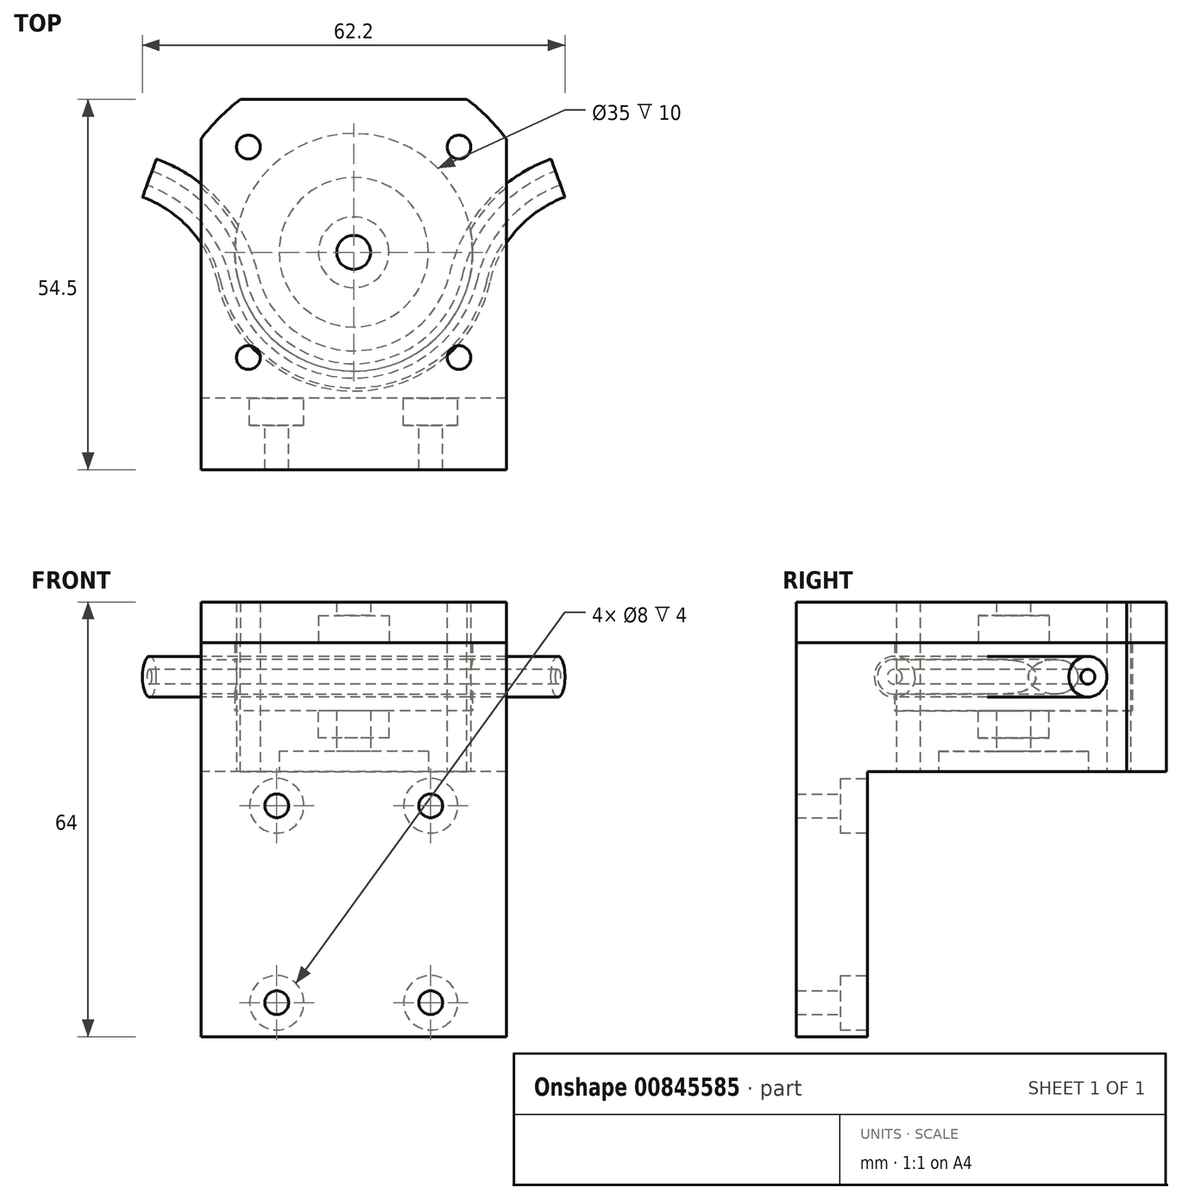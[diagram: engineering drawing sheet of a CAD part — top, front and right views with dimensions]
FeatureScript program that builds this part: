
annotation { "Feature Type Name" : "Feature", "Feature Type Description" : "" }
export const myFeature = defineFeature(function(context is Context, id is Id, definition is map)
    precondition{}
    {
        {
            var Q0;
            Q0=qCreatedBy(makeId("Top.planeOp"),FACE);
            var sketch = newSketch(context, id + "F0", { "sketchPlane" : qUnion([Q0])});
            skLineSegment(sketch, "E0", {"start": v(-21.5, -16.33) * mm, "end": v(-21.5, 16.33) * mm});
            skLineSegment(sketch, "E1", {"start": v(-16.33, 21.5) * mm, "end": v(16.33, 21.5) * mm});
            skLineSegment(sketch, "E2", {"start": v(21.5, 16.33) * mm, "end": v(21.5, -16.33) * mm});
            skLineSegment(sketch, "E3", {"start": v(16.33, -21.5) * mm, "end": v(-16.33, -21.5) * mm});
            skArc(sketch, "E4", {"start": v(-16.33, 21.5) * mm, "mid": v(-19.1, 19.1) * mm, "end": v(-21.5, 16.33) * mm});
            skArc(sketch, "E5", {"start": v(21.5, 16.33) * mm, "mid": v(19.1, 19.1) * mm, "end": v(16.33, 21.5) * mm});
            skCircle(sketch, "E6", {"center": v(-15.5, 15.5) * mm, "radius": 1.75 * mm});
            skCircle(sketch, "E7", {"center": v(15.5, 15.5) * mm, "radius": 1.75 * mm});
            skCircle(sketch, "E8", {"center": v(0, 0) * mm, "radius": 11 * mm});
            skCircle(sketch, "E9", {"center": v(-15.5, -15.5) * mm, "radius": 1.75 * mm});
            skCircle(sketch, "E10", {"center": v(15.5, -15.5) * mm, "radius": 1.75 * mm});
            skArc(sketch, "E11", {"start": v(-21.5, -16.33) * mm, "mid": v(-19.1, -19.1) * mm, "end": v(-16.33, -21.5) * mm});
            skArc(sketch, "E12", {"start": v(16.33, -21.5) * mm, "mid": v(19.1, -19.1) * mm, "end": v(21.5, -16.33) * mm});
            skLineSegment(sketch, "E13.bottom", {"start": v(15.5, 15.5) * mm, "end": v(-15.5, 15.5) * mm, "construction": true});
            skLineSegment(sketch, "E13.top", {"start": v(15.5, -15.5) * mm, "end": v(-15.5, -15.5) * mm, "construction": true});
            skLineSegment(sketch, "E13.left", {"start": v(15.5, 15.5) * mm, "end": v(15.5, -15.5) * mm, "construction": true});
            skLineSegment(sketch, "E13.right", {"start": v(-15.5, 15.5) * mm, "end": v(-15.5, -15.5) * mm, "construction": true});
            skLineSegment(sketch, "E14", {"start": v(0, 21.5) * mm, "end": v(0, -21.5) * mm, "construction": true});
            skLineSegment(sketch, "E15", {"start": v(-21.5, 0) * mm, "end": v(21.5, 0) * mm, "construction": true});
            skPoint(sketch, "E15.endSnap0", {"position": v(21.5, 0) * mm});
            skCircle(sketch, "E16", {"center": v(0, 0) * mm, "radius": 2.5 * mm});
            skSolve(sketch);
        }
        {
            var Q0;
            Q0=makeQuery(id+"F0.imprint","IMPRINT",FACE,{"disambiguationData":[TD([[makeQuery(id+"F0.imprint","IMPRINT",EDGE,{"derivedFrom":sQuery(id+"F0.wireOp",EDGE,"E0")}),-1.0]])]});
            var Q1;
            Q1=makeQuery(id+"F0.imprint","IMPRINT",FACE,{"disambiguationData":[TD([[makeQuery(id+"F0.imprint","IMPRINT",EDGE,{"derivedFrom":sQuery(id+"F0.wireOp",EDGE,"E8")}),1.0]])]});
            extrude(context, id + "F1", {"entities" : qUnion([Q0, Q1]), "depth" : 2 * mm, "offsetDistance" : 25 * mm});
        }
        {
            var Q0;
            Q0=makeQuery(id+"F1.opExtrude","CAP_FACE",FACE,{"disambiguationData":[OSD([sQuery(id+"F0.wireOp",EDGE,"E0"),sQuery(id+"F0.wireOp",EDGE,"E1"),sQuery(id+"F0.wireOp",EDGE,"E2"),sQuery(id+"F0.wireOp",EDGE,"E3"),sQuery(id+"F0.wireOp",EDGE,"E4"),sQuery(id+"F0.wireOp",EDGE,"E5"),sQuery(id+"F0.wireOp",EDGE,"E6"),sQuery(id+"F0.wireOp",EDGE,"E7"),sQuery(id+"F0.wireOp",EDGE,"E8"),sQuery(id+"F0.wireOp",EDGE,"E9"),sQuery(id+"F0.wireOp",EDGE,"E10"),sQuery(id+"F0.wireOp",EDGE,"E11"),sQuery(id+"F0.wireOp",EDGE,"E12")])],"isStart":false});
            var Q1;
            Q1=makeQuery(id+"F0.imprint","IMPRINT",FACE,{"disambiguationData":[TD([[makeQuery(id+"F0.imprint","IMPRINT",EDGE,{"derivedFrom":sQuery(id+"F0.wireOp",EDGE,"d85fea0c-31e0-45f3-b9b2-28f0fcc0159b")}),-1.0]])]});
            extrude(context, id + "F2", {"entities" : qUnion([Q0, Q1]), "operationType" : NewBodyOperationType.ADD, "depth" : 7 * mm, "offsetDistance" : 25 * mm});
        }
        {
            var Q0;
            Q0=makeQuery(id+"F2.opExtrude","CAP_FACE",FACE,{"disambiguationData":[OSD([sQuery(id+"F0.wireOp",EDGE,"E0"),sQuery(id+"F0.wireOp",EDGE,"E1"),sQuery(id+"F0.wireOp",EDGE,"E2"),sQuery(id+"F0.wireOp",EDGE,"E3"),sQuery(id+"F0.wireOp",EDGE,"E4"),sQuery(id+"F0.wireOp",EDGE,"E5"),sQuery(id+"F0.wireOp",EDGE,"E6"),sQuery(id+"F0.wireOp",EDGE,"E7"),sQuery(id+"F0.wireOp",EDGE,"E8"),sQuery(id+"F0.wireOp",EDGE,"E9"),sQuery(id+"F0.wireOp",EDGE,"E10"),sQuery(id+"F0.wireOp",EDGE,"E11"),sQuery(id+"F0.wireOp",EDGE,"E12")])],"isStart":false});
            var sketch = newSketch(context, id + "F3", { "sketchPlane" : qUnion([Q0])});
            skArc(sketch, "E17.0", {"start": v(-16.67, 22.5) * mm, "mid": v(-19.8, 19.8) * mm, "end": v(-22.5, 16.67) * mm});
            skLineSegment(sketch, "E17.1", {"start": v(-22.5, -16.67) * mm, "end": v(-22.5, 16.67) * mm});
            skLineSegment(sketch, "E17.2", {"start": v(-16.67, 22.5) * mm, "end": v(16.67, 22.5) * mm});
            skArc(sketch, "E17.3", {"start": v(-22.5, -16.67) * mm, "mid": v(-19.8, -19.8) * mm, "end": v(-16.67, -22.5) * mm});
            skArc(sketch, "E17.4", {"start": v(22.5, 16.67) * mm, "mid": v(19.8, 19.8) * mm, "end": v(16.67, 22.5) * mm});
            skLineSegment(sketch, "E17.5", {"start": v(22.5, 16.67) * mm, "end": v(22.5, -16.67) * mm});
            skArc(sketch, "E17.6", {"start": v(16.67, -22.5) * mm, "mid": v(19.8, -19.8) * mm, "end": v(22.5, -16.67) * mm});
            skLineSegment(sketch, "E17.7", {"start": v(16.67, -22.5) * mm, "end": v(-16.67, -22.5) * mm});
            skSolve(sketch);
        }
        {
            var Q0;
            Q0=makeQuery(id+"F3.imprint","IMPRINT",FACE,{"disambiguationData":[TD([[makeQuery(id+"F3.imprint","IMPRINT",EDGE,{"derivedFrom":sQuery(id+"F3.wireOp",EDGE,"E17.0")}),1.0]])]});
            extrude(context, id + "F4", {"entities" : qUnion([Q0]), "operationType" : NewBodyOperationType.ADD, "oppositeDirection" : true, "depth" : 48 * mm, "offsetDistance" : 25 * mm});
        }
        {
            var Q0;
            {var subQ0=sQuery(id+"F0.wireOp",EDGE,"E12");var subQ1=sQuery(id+"F0.wireOp",EDGE,"E11");var subQ2=sQuery(id+"F0.wireOp",EDGE,"E5");var subQ3=sQuery(id+"F0.wireOp",EDGE,"E4");var subQ4=sQuery(id+"F0.wireOp",EDGE,"E3");var subQ5=sQuery(id+"F0.wireOp",EDGE,"E2");var subQ6=sQuery(id+"F0.wireOp",EDGE,"E1");var subQ7=sQuery(id+"F0.wireOp",EDGE,"E0");Q0=makeQuery(id+"F4.boolean.opBoolean","MERGE",FACE,{"derivedFrom":[makeQuery(id+"F2.opExtrude","CAP_FACE",FACE,{"disambiguationData":[OSD([subQ7,subQ6,subQ5,subQ4,subQ3,subQ2,sQuery(id+"F0.wireOp",EDGE,"E6"),sQuery(id+"F0.wireOp",EDGE,"E7"),sQuery(id+"F0.wireOp",EDGE,"E8"),sQuery(id+"F0.wireOp",EDGE,"E9"),sQuery(id+"F0.wireOp",EDGE,"E10"),subQ1,subQ0])],"isStart":false}),makeQuery(id+"F4.opExtrude","CAP_FACE",FACE,{"disambiguationData":[OSD([subQ7,subQ6,subQ5,subQ4,subQ3,subQ2,subQ1,subQ0,sQuery(id+"F3.wireOp",EDGE,"E17.0"),sQuery(id+"F3.wireOp",EDGE,"E17.1"),sQuery(id+"F3.wireOp",EDGE,"E17.2"),sQuery(id+"F3.wireOp",EDGE,"E17.3"),sQuery(id+"F3.wireOp",EDGE,"E17.4"),sQuery(id+"F3.wireOp",EDGE,"E17.5"),sQuery(id+"F3.wireOp",EDGE,"E17.6"),sQuery(id+"F3.wireOp",EDGE,"E17.7")])],"isStart":true})]});}
            var sketch = newSketch(context, id + "F5", { "sketchPlane" : qUnion([Q0])});
            skCircle(sketch, "E18", {"center": v(0, 0) * mm, "radius": 32 * mm});
            skLineSegment(sketch, "E19", {"start": v(-22.5, -16.67) * mm, "end": v(-22.5, -32) * mm});
            skLineSegment(sketch, "E20", {"start": v(-22.5, -32) * mm, "end": v(22.5, -32) * mm});
            skLineSegment(sketch, "E21", {"start": v(22.5, -32) * mm, "end": v(22.5, -16.67) * mm});
            skCircle(sketch, "E22", {"center": v(0, 0) * mm, "radius": 17.5 * mm});
            skCircle(sketch, "E23", {"center": v(0, 0) * mm, "radius": 2.5 * mm});
            skSolve(sketch);
        }
        {
            var Q0;
            {var subQ1=sQuery(id+"F5.wireOp",EDGE,"E21");Q0=makeQuery(id+"F5.imprint","IMPRINT",FACE,{"disambiguationData":[TD([[makeQuery(id+"F5.imprint","IMPRINT",EDGE,{"derivedFrom":subQ1}),1.0]])]});}
            var Q1;
            {var subQ1=sQuery(id+"F5.wireOp",EDGE,"E19");Q1=makeQuery(id+"F5.imprint","IMPRINT",FACE,{"disambiguationData":[TD([[makeQuery(id+"F5.imprint","IMPRINT",EDGE,{"derivedFrom":subQ1}),1.0]])]});}
            var Q2;
            {var subQ0=sQuery(id+"F5.wireOp",EDGE,"E18");var subQ1=makeQuery(id+"F5.imprint","INTERSECT",VERTEX,{"derivedFrom":[subQ0,sQuery(id+"F5.wireOp",EDGE,"E20")]});Q2=makeQuery(id+"F5.imprint","IMPRINT",FACE,{"disambiguationData":[TD([[makeQuery(id+"F5.imprint","IMPRINT",EDGE,{"disambiguationData":[TD([[subQ1,1.0]])],"derivedFrom":subQ0}),1.0]])]});}
            extrude(context, id + "F6", {"entities" : qUnion([Q0, Q1, Q2]), "operationType" : NewBodyOperationType.ADD, "oppositeDirection" : true, "depth" : 48 * mm, "offsetDistance" : 25 * mm});
        }
        {
            var Q0;
            {var subQ4=sQuery(id+"F5.wireOp",EDGE,"E18");var subQ28=makeQuery(id+"F4.opExtrude","CAP_EDGE",EDGE,{"disambiguationData":[OSD([sQuery(id+"F3.wireOp",EDGE,"646ab015-f94a-48a6-a4ab-2b46942ccab2.2")])],"isStart":true});var subQ29=makeQuery(id+"F5.imprint","INTERSECT",VERTEX,{"derivedFrom":[subQ28,subQ4]});Q0=makeQuery(id+"F5.imprint","IMPRINT",FACE,{"disambiguationData":[TD([[makeQuery(id+"F5.imprint","IMPRINT",EDGE,{"disambiguationData":[TD([[subQ29,-1.0]])],"derivedFrom":subQ4}),1.0]])]});}
            var Q1;
            {var subQ0=sQuery(id+"F5.wireOp",EDGE,"E18");var subQ1=makeQuery(id+"F4.boolean.opBoolean","MERGE",EDGE,{"derivedFrom":[makeQuery(id+"F2.opExtrude","CAP_EDGE",EDGE,{"disambiguationData":[OSD([sQuery(id+"F1Hpu5VrwMmlooL_1.wireOp",EDGE,"8e26481d-0692-495c-8b6e-13f98c5af57d")])],"isStart":false}),makeQuery(id+"F4.opExtrude","CAP_EDGE",EDGE,{"disambiguationData":[OSD([sQuery(id+"F3.wireOp",EDGE,"JSha1XCR-3J3x-jMRG-RlZc-dtnEwsOd18PA")])],"isStart":true}),makeQuery(id+"F4.opExtrude","CAP_EDGE",EDGE,{"disambiguationData":[OSD([sQuery(id+"F3.wireOp",EDGE,"9211a1b2-c39d-4ab5-b8c2-9bb960df69d4.trimOffspring")])],"isStart":true})]});var subQ2=makeQuery(id+"F5.imprint","INTERSECT",VERTEX,{"disambiguationData":[OD(0.0)],"derivedFrom":[subQ1,subQ0]});Q1=makeQuery(id+"F5.imprint","IMPRINT",FACE,{"disambiguationData":[TD([[makeQuery(id+"F5.imprint","IMPRINT",EDGE,{"disambiguationData":[TD([[subQ2,-1.0]])],"derivedFrom":subQ0}),1.0]])]});}
            var Q2;
            {var subQ0=sQuery(id+"F5.wireOp",EDGE,"E18");var subQ1=makeQuery(id+"F4.opExtrude","CAP_EDGE",EDGE,{"disambiguationData":[OSD([sQuery(id+"F3.wireOp",EDGE,"646ab015-f94a-48a6-a4ab-2b46942ccab2.4")])],"isStart":true});var subQ2=makeQuery(id+"F5.imprint","INTERSECT",VERTEX,{"derivedFrom":[subQ1,subQ0]});Q2=makeQuery(id+"F5.imprint","IMPRINT",FACE,{"disambiguationData":[TD([[makeQuery(id+"F5.imprint","IMPRINT",EDGE,{"disambiguationData":[TD([[subQ2,-1.0]])],"derivedFrom":subQ0}),1.0]])]});}
            var Q3;
            {var subQ6=sQuery(id+"F5.wireOp",EDGE,"E19");Q3=makeQuery(id+"F5.imprint","IMPRINT",FACE,{"disambiguationData":[TD([[makeQuery(id+"F5.imprint","IMPRINT",EDGE,{"derivedFrom":subQ6}),1.0]])]});}
            var Q4;
            {var subQ0=sQuery(id+"F5.wireOp",EDGE,"E18");var subQ1=makeQuery(id+"F5.imprint","INTERSECT",VERTEX,{"derivedFrom":[subQ0,sQuery(id+"F5.wireOp",EDGE,"E20")]});Q4=makeQuery(id+"F5.imprint","IMPRINT",FACE,{"disambiguationData":[TD([[makeQuery(id+"F5.imprint","IMPRINT",EDGE,{"disambiguationData":[TD([[subQ1,1.0]])],"derivedFrom":subQ0}),1.0]])]});}
            var Q5;
            {var subQ6=sQuery(id+"F5.wireOp",EDGE,"E21");Q5=makeQuery(id+"F5.imprint","IMPRINT",FACE,{"disambiguationData":[TD([[makeQuery(id+"F5.imprint","IMPRINT",EDGE,{"derivedFrom":subQ6}),1.0]])]});}
            var Q6;
            {var subQ0=sQuery(id+"F5.wireOp",EDGE,"E18");var subQ1=makeQuery(id+"F4.opExtrude","CAP_EDGE",EDGE,{"disambiguationData":[OSD([sQuery(id+"F3.wireOp",EDGE,"646ab015-f94a-48a6-a4ab-2b46942ccab2.7")])],"isStart":true});var subQ2=makeQuery(id+"F5.imprint","INTERSECT",VERTEX,{"disambiguationData":[OD(0.0)],"derivedFrom":[subQ1,subQ0]});Q6=makeQuery(id+"F5.imprint","IMPRINT",FACE,{"disambiguationData":[TD([[makeQuery(id+"F5.imprint","IMPRINT",EDGE,{"disambiguationData":[TD([[subQ2,1.0]])],"derivedFrom":subQ0}),1.0]])]});}
            var Q7;
            {var subQ0=sQuery(id+"F5.wireOp",EDGE,"E22");var subQ1=makeQuery(id+"F2.opExtrude","CAP_EDGE",EDGE,{"disambiguationData":[OSD([sQuery(id+"F1Hpu5VrwMmlooL_1.wireOp",EDGE,"9a130dde-bc44-4270-aeb8-7f362e7485a4")])],"isStart":false});var subQ2=makeQuery(id+"F5.imprint","INTERSECT",VERTEX,{"disambiguationData":[OD(0.0)],"derivedFrom":[subQ1,subQ0]});Q7=makeQuery(id+"F5.imprint","IMPRINT",FACE,{"disambiguationData":[TD([[makeQuery(id+"F5.imprint","IMPRINT",EDGE,{"disambiguationData":[TD([[subQ2,-1.0]])],"derivedFrom":subQ0}),-1.0]])]});}
            var Q8;
            {var subQ0=sQuery(id+"F5.wireOp",EDGE,"E22");var subQ1=makeQuery(id+"F2.opExtrude","CAP_EDGE",EDGE,{"disambiguationData":[OSD([sQuery(id+"F1Hpu5VrwMmlooL_1.wireOp",EDGE,"1fc29757-d1f2-4ccb-9a81-5a1ceaa807c7")])],"isStart":false});var subQ2=makeQuery(id+"F5.imprint","INTERSECT",VERTEX,{"disambiguationData":[OD(0.0)],"derivedFrom":[subQ1,subQ0]});Q8=makeQuery(id+"F5.imprint","IMPRINT",FACE,{"disambiguationData":[TD([[makeQuery(id+"F5.imprint","IMPRINT",EDGE,{"disambiguationData":[TD([[subQ2,-1.0]])],"derivedFrom":subQ0}),-1.0]])]});}
            var Q9;
            {var subQ0=sQuery(id+"F5.wireOp",EDGE,"E22");var subQ1=makeQuery(id+"F2.opExtrude","CAP_EDGE",EDGE,{"disambiguationData":[OSD([sQuery(id+"F1Hpu5VrwMmlooL_1.wireOp",EDGE,"4d534888-ec9c-4465-8bad-2fd676ba325a")])],"isStart":false});var subQ2=makeQuery(id+"F5.imprint","INTERSECT",VERTEX,{"disambiguationData":[OD(0.0)],"derivedFrom":[subQ1,subQ0]});Q9=makeQuery(id+"F5.imprint","IMPRINT",FACE,{"disambiguationData":[TD([[makeQuery(id+"F5.imprint","IMPRINT",EDGE,{"disambiguationData":[TD([[subQ2,1.0]])],"derivedFrom":subQ0}),-1.0]])]});}
            var Q10;
            {var subQ0=sQuery(id+"F5.wireOp",EDGE,"E22");var subQ1=makeQuery(id+"F2.opExtrude","CAP_EDGE",EDGE,{"disambiguationData":[OSD([sQuery(id+"F1Hpu5VrwMmlooL_1.wireOp",EDGE,"5fe68f5a-298d-45ce-920e-f32339d6a1d9")])],"isStart":false});var subQ2=makeQuery(id+"F5.imprint","INTERSECT",VERTEX,{"disambiguationData":[OD(0.0)],"derivedFrom":[subQ1,subQ0]});Q10=makeQuery(id+"F5.imprint","IMPRINT",FACE,{"disambiguationData":[TD([[makeQuery(id+"F5.imprint","IMPRINT",EDGE,{"disambiguationData":[TD([[subQ2,-1.0]])],"derivedFrom":subQ0}),-1.0]])]});}
            var Q11;
            Q11=makeQuery(id+"F5.imprint","IMPRINT",FACE,{"disambiguationData":[TD([[makeQuery(id+"F5.imprint","IMPRINT",EDGE,{"derivedFrom":sQuery(id+"F5.wireOp",EDGE,"E22")}),-1.0]])]});
            extrude(context, id + "F7", {"entities" : qUnion([Q0, Q1, Q2, Q3, Q4, Q5, Q6, Q7, Q8, Q9, Q10, Q11]), "operationType" : NewBodyOperationType.ADD, "depth" : 10 * mm, "offsetDistance" : 25 * mm});
        }
        {
            var Q0;
            {var subQ4=sQuery(id+"F5.wireOp",EDGE,"E18");var subQ28=makeQuery(id+"F4.opExtrude","CAP_EDGE",EDGE,{"disambiguationData":[OSD([sQuery(id+"F3.wireOp",EDGE,"646ab015-f94a-48a6-a4ab-2b46942ccab2.2")])],"isStart":true});var subQ29=makeQuery(id+"F5.imprint","INTERSECT",VERTEX,{"derivedFrom":[subQ28,subQ4]});Q0=makeQuery(id+"F5.imprint","IMPRINT",FACE,{"disambiguationData":[TD([[makeQuery(id+"F5.imprint","IMPRINT",EDGE,{"disambiguationData":[TD([[subQ29,-1.0]])],"derivedFrom":subQ4}),1.0]])]});}
            cPlane(context, id + "F8", {"entities" : qUnion([Q0]), "cplaneType" : CPlaneType.OFFSET, "offset" : 5 * mm, "width" : 150 * mm, "height" : 150 * mm});
        }
        {
            var Q0;
            Q0=qCreatedBy(id+"F8.planeOp",FACE);
            var sketch = newSketch(context, id + "F9", { "sketchPlane" : qUnion([Q0])});
            skArc(sketch, "E24", {"start": v(-17.07, -3.83) * mm, "mid": v(0, -17.5) * mm, "end": v(17.07, -3.83) * mm});
            skArc(sketch, "E25", {"start": v(-17.07, -3.83) * mm, "mid": v(-21.68, 5.22) * mm, "end": v(-30.07, 10.94) * mm});
            skArc(sketch, "E26", {"start": v(30.07, 10.94) * mm, "mid": v(21.68, 5.22) * mm, "end": v(17.07, -3.83) * mm});
            skLineSegment(sketch, "E27", {"start": v(0, 0) * mm, "end": v(30.07, 10.94) * mm, "construction": true});
            skLineSegment(sketch, "E28", {"start": v(0, 0) * mm, "end": v(-30.07, 10.94) * mm, "construction": true});
            skLineSegment(sketch, "E29", {"start": v(-34.05, 0) * mm, "end": v(34.05, 0) * mm, "construction": true});
            skLineSegment(sketch, "E30", {"start": v(-30.07, 10.94) * mm, "end": v(-34.05, 0) * mm, "construction": true});
            skLineSegment(sketch, "E31", {"start": v(30.07, 10.94) * mm, "end": v(34.05, 0) * mm, "construction": true});
            skSolve(sketch);
        }
        {
            var Q0;
            Q0=sQuery(id+"F9.wireOp",EDGE,"E30");
            cPlane(context, id + "F10", {"entities" : qUnion([Q0]), "cplaneType" : CPlaneType.LINE_ANGLE, "offset" : 0 * mm, "angle" : 90 * degree, "width" : 150 * mm, "height" : 150 * mm});
        }
        {
            var Q0;
            Q0=qCreatedBy(id+"F10.planeOp",FACE);
            var sketch = newSketch(context, id + "F11", { "sketchPlane" : qUnion([Q0])});
            skCircle(sketch, "E32", {"center": v(0, 14) * mm, "radius": 3 * mm});
            skCircle(sketch, "E33", {"center": v(0, 14) * mm, "radius": 1.1 * mm});
            skSolve(sketch);
        }
        {
            var Q0;
            Q0=sQuery(id+"F9.wireOp",EDGE,"E31");
            cPlane(context, id + "F12", {"entities" : qUnion([Q0]), "cplaneType" : CPlaneType.LINE_ANGLE, "offset" : 2.5 * mm, "angle" : 90 * degree, "width" : 150 * mm, "height" : 150 * mm});
        }
        {
            var Q0;
            Q0=qCreatedBy(id+"F12.planeOp",FACE);
            var sketch = newSketch(context, id + "F13", { "sketchPlane" : qUnion([Q0])});
            skCircle(sketch, "E34", {"center": v(0, 14) * mm, "radius": 2.55 * mm});
            skSolve(sketch);
        }
        {
            var Q0;
            Q0=makeQuery(id+"F13.imprint","IMPRINT",FACE,{"disambiguationData":[TD([[makeQuery(id+"F13.imprint","IMPRINT",EDGE,{"derivedFrom":sQuery(id+"F13.wireOp",EDGE,"E34")}),1.0]])]});
            var Q1;
            Q1=qConstructionFilter(qBodyType(qCreatedBy(id+"F9",EDGE),BodyType.WIRE),ConstructionObject.NO);
            sweep(context, id + "F14", {"operationType" : NewBodyOperationType.REMOVE, "profiles" : qUnion([Q0]), "path" : qUnion([Q1])});
        }
        {
            var Q0;
            Q0=makeQuery(id+"F7.opExtrude","CAP_FACE",FACE,{"disambiguationData":[OSD([sQuery(id+"F3.wireOp",EDGE,"646ab015-f94a-48a6-a4ab-2b46942ccab2.0"),sQuery(id+"F3.wireOp",EDGE,"646ab015-f94a-48a6-a4ab-2b46942ccab2.1"),sQuery(id+"F3.wireOp",EDGE,"646ab015-f94a-48a6-a4ab-2b46942ccab2.3"),sQuery(id+"F5.wireOp",EDGE,"E18"),sQuery(id+"F5.wireOp",EDGE,"E19"),sQuery(id+"F5.wireOp",EDGE,"E20"),sQuery(id+"F5.wireOp",EDGE,"E21"),sQuery(id+"F5.wireOp",EDGE,"E22")])],"isStart":false});
            var sketch = newSketch(context, id + "F15", { "sketchPlane" : qUnion([Q0])});
            skCircle(sketch, "E35", {"center": v(0, 0) * mm, "radius": 31.47 * mm});
            skCircle(sketch, "E36", {"center": v(0, 0) * mm, "radius": 2.5 * mm});
            skSolve(sketch);
        }
        {
            var Q0;
            Q0=makeQuery(id+"F15.imprint","IMPRINT",FACE,{"disambiguationData":[TD([[makeQuery(id+"F15.imprint","IMPRINT",EDGE,{"derivedFrom":sQuery(id+"F15.wireOp",EDGE,"E36")}),-1.0]])]});
            var Q1;
            Q1=makeQuery(id+"F15.imprint","IMPRINT",FACE,{"disambiguationData":[TD([[makeQuery(id+"F15.imprint","IMPRINT",EDGE,{"derivedFrom":makeQuery(id+"F7.opExtrude","CAP_EDGE",EDGE,{"disambiguationData":[OSD([sQuery(id+"F5.wireOp",EDGE,"E22")])],"isStart":false})}),-1.0]])]});
            var Q2;
            {var subQ5=makeQuery(id+"F7.opExtrude","CAP_EDGE",EDGE,{"disambiguationData":[OSD([sQuery(id+"F5.wireOp",EDGE,"E20")])],"isStart":false});Q2=makeQuery(id+"F15.imprint","IMPRINT",FACE,{"disambiguationData":[TD([[makeQuery(id+"F15.imprint","IMPRINT",EDGE,{"derivedFrom":subQ5}),1.0]])]});}
            var Q3;
            {var subQ1=sQuery(id+"F3.wireOp",EDGE,"E17.2");var subQ7=sQuery(id+"F5.wireOp",EDGE,"E18");var subQ8=makeQuery(id+"F7.opExtrude","CAP_EDGE",EDGE,{"disambiguationData":[OSD([subQ7]),TDD([makeQuery(id+"F5.imprint","IMPRINT",EDGE,{"disambiguationData":[TD([[makeQuery(id+"F5.imprint","INTERSECT",VERTEX,{"disambiguationData":[OD(1.0)],"derivedFrom":[makeQuery(id+"F4.opExtrude","CAP_EDGE",EDGE,{"disambiguationData":[OSD([subQ1])],"isStart":true}),subQ7]}),1.0]])],"derivedFrom":subQ7})])],"isStart":false});Q3=makeQuery(id+"F15.imprint","IMPRINT",FACE,{"disambiguationData":[TD([[makeQuery(id+"F15.imprint","IMPRINT",EDGE,{"derivedFrom":subQ8}),1.0]])]});}
            var Q4;
            {var subQ1=sQuery(id+"F3.wireOp",EDGE,"E17.2");var subQ7=sQuery(id+"F5.wireOp",EDGE,"E18");var subQ8=makeQuery(id+"F7.opExtrude","CAP_EDGE",EDGE,{"disambiguationData":[OSD([subQ7]),TDD([makeQuery(id+"F5.imprint","IMPRINT",EDGE,{"disambiguationData":[TD([[makeQuery(id+"F5.imprint","INTERSECT",VERTEX,{"disambiguationData":[OD(0.0)],"derivedFrom":[makeQuery(id+"F4.opExtrude","CAP_EDGE",EDGE,{"disambiguationData":[OSD([subQ1])],"isStart":true}),subQ7]}),-1.0]])],"derivedFrom":subQ7})])],"isStart":false});Q4=makeQuery(id+"F15.imprint","IMPRINT",FACE,{"disambiguationData":[TD([[makeQuery(id+"F15.imprint","IMPRINT",EDGE,{"derivedFrom":subQ8}),1.0]])]});}
            extrude(context, id + "F16", {"entities" : qUnion([Q0, Q1, Q2, Q3, Q4]), "depth" : 6 * mm, "offsetDistance" : 25 * mm});
        }
        {
            var Q0;
            Q0=makeQuery(id+"F16.opExtrude","CAP_FACE",FACE,{"disambiguationData":[OSD([sQuery(id+"F1Hpu5VrwMmlooL_1.wireOp",EDGE,"8e26481d-0692-495c-8b6e-13f98c5af57d"),sQuery(id+"F1Hpu5VrwMmlooL_1.wireOp",EDGE,"5fe68f5a-298d-45ce-920e-f32339d6a1d9"),sQuery(id+"F1Hpu5VrwMmlooL_1.wireOp",EDGE,"4d534888-ec9c-4465-8bad-2fd676ba325a"),sQuery(id+"F1Hpu5VrwMmlooL_1.wireOp",EDGE,"9a130dde-bc44-4270-aeb8-7f362e7485a4"),sQuery(id+"F1Hpu5VrwMmlooL_1.wireOp",EDGE,"1fc29757-d1f2-4ccb-9a81-5a1ceaa807c7"),sQuery(id+"F3.wireOp",EDGE,"646ab015-f94a-48a6-a4ab-2b46942ccab2.2"),sQuery(id+"F3.wireOp",EDGE,"646ab015-f94a-48a6-a4ab-2b46942ccab2.4"),sQuery(id+"F3.wireOp",EDGE,"646ab015-f94a-48a6-a4ab-2b46942ccab2.7"),sQuery(id+"F3.wireOp",EDGE,"JSha1XCR-3J3x-jMRG-RlZc-dtnEwsOd18PA"),sQuery(id+"F3.wireOp",EDGE,"9211a1b2-c39d-4ab5-b8c2-9bb960df69d4.trimOffspring"),sQuery(id+"F5.wireOp",EDGE,"E19"),sQuery(id+"F5.wireOp",EDGE,"E20"),sQuery(id+"F5.wireOp",EDGE,"E21"),sQuery(id+"F15.wireOp",EDGE,"E35"),sQuery(id+"F15.wireOp",EDGE,"E36")])],"isStart":true});
            var sketch = newSketch(context, id + "F17", { "sketchPlane" : qUnion([Q0])});
            skCircle(sketch, "E37", {"center": v(0, 0) * mm, "radius": 5.2 * mm});
            skSolve(sketch);
        }
        {
            var Q0;
            Q0=makeQuery(id+"F17.imprint","IMPRINT",FACE,{"disambiguationData":[TD([[makeQuery(id+"F17.imprint","IMPRINT",EDGE,{"derivedFrom":sQuery(id+"F17.wireOp",EDGE,"E37")}),1.0]])]});
            extrude(context, id + "F18", {"entities" : qUnion([Q0]), "operationType" : NewBodyOperationType.REMOVE, "oppositeDirection" : true, "depth" : 4 * mm, "offsetDistance" : 25 * mm});
        }
        {
            var Q0;
            {var subQ0=sQuery(id+"F3.wireOp",EDGE,"646ab015-f94a-48a6-a4ab-2b46942ccab2.3");var subQ1=sQuery(id+"F3.wireOp",EDGE,"646ab015-f94a-48a6-a4ab-2b46942ccab2.1");var subQ2=sQuery(id+"F3.wireOp",EDGE,"646ab015-f94a-48a6-a4ab-2b46942ccab2.0");Q0=makeQuery(id+"F6.boolean.opBoolean","MERGE",FACE,{"derivedFrom":[makeQuery(id+"F4.boolean.opBoolean","MERGE",FACE,{"derivedFrom":[makeQuery(id+"F2.opExtrude","CAP_FACE",FACE,{"disambiguationData":[OSD([sQuery(id+"F1Hpu5VrwMmlooL_1.wireOp",EDGE,"bdebe98e-508b-4dc6-81ce-e9b0915b905b"),sQuery(id+"F1Hpu5VrwMmlooL_1.wireOp",EDGE,"8e26481d-0692-495c-8b6e-13f98c5af57d"),sQuery(id+"F1Hpu5VrwMmlooL_1.wireOp",EDGE,"730d604f-0751-4adf-84c4-564d4acc1bf2"),sQuery(id+"F1Hpu5VrwMmlooL_1.wireOp",EDGE,"3ae73026-240c-434e-8128-a4e5a43a5ace"),sQuery(id+"F1Hpu5VrwMmlooL_1.wireOp",EDGE,"67bd35a3-ead6-4aac-8275-85918547268a"),sQuery(id+"F1Hpu5VrwMmlooL_1.wireOp",EDGE,"ca31c680-71a9-4e06-93d3-dcdf511aacea"),sQuery(id+"F1Hpu5VrwMmlooL_1.wireOp",EDGE,"5fe68f5a-298d-45ce-920e-f32339d6a1d9"),sQuery(id+"F1Hpu5VrwMmlooL_1.wireOp",EDGE,"4d534888-ec9c-4465-8bad-2fd676ba325a"),sQuery(id+"F1Hpu5VrwMmlooL_1.wireOp",EDGE,"9a130dde-bc44-4270-aeb8-7f362e7485a4"),sQuery(id+"F1Hpu5VrwMmlooL_1.wireOp",EDGE,"1fc29757-d1f2-4ccb-9a81-5a1ceaa807c7"),sQuery(id+"F1Hpu5VrwMmlooL_1.wireOp",EDGE,"e0ca1a5b-4a5a-4701-b7b4-a9afa6e3c82b"),sQuery(id+"F1Hpu5VrwMmlooL_1.wireOp",EDGE,"f9228ba7-bf05-45cf-b3cc-3e8c137fda38"),sQuery(id+"F1Hpu5VrwMmlooL_1.wireOp",EDGE,"aa8661ea-3af5-4901-8aae-093f1f5eb203")])],"isStart":false}),makeQuery(id+"F4.opExtrude","CAP_FACE",FACE,{"disambiguationData":[OSD([sQuery(id+"F3.wireOp",EDGE,"3a0f54d8-991b-4f62-906c-7d67a353449a"),sQuery(id+"F3.wireOp",EDGE,"98a7e771-4bfb-4205-8b27-0b6975573ff0"),sQuery(id+"F3.wireOp",EDGE,"4c77cdeb-d146-4bfc-8ccc-5c3fcd001468"),sQuery(id+"F3.wireOp",EDGE,"460aea3b-1a94-4910-b809-b134830fa8c7"),sQuery(id+"F3.wireOp",EDGE,"872af010-c28f-43d9-90a7-629491c90a93"),sQuery(id+"F3.wireOp",EDGE,"7882bdaf-68c7-4416-8fdf-58388a205b18"),sQuery(id+"F3.wireOp",EDGE,"9d6daaff-0767-4eaf-b26b-b552bb5ee980"),subQ2,subQ1,sQuery(id+"F3.wireOp",EDGE,"646ab015-f94a-48a6-a4ab-2b46942ccab2.2"),subQ0,sQuery(id+"F3.wireOp",EDGE,"646ab015-f94a-48a6-a4ab-2b46942ccab2.4"),sQuery(id+"F3.wireOp",EDGE,"646ab015-f94a-48a6-a4ab-2b46942ccab2.6"),sQuery(id+"F3.wireOp",EDGE,"646ab015-f94a-48a6-a4ab-2b46942ccab2.7"),sQuery(id+"F3.wireOp",EDGE,"JSha1XCR-3J3x-jMRG-RlZc-dtnEwsOd18PA"),sQuery(id+"F3.wireOp",EDGE,"9211a1b2-c39d-4ab5-b8c2-9bb960df69d4.trimOffspring")])],"isStart":true})]}),makeQuery(id+"F6.opExtrude","CAP_FACE",FACE,{"disambiguationData":[OSD([subQ2,subQ1,subQ0,sQuery(id+"F5.wireOp",EDGE,"E19"),sQuery(id+"F5.wireOp",EDGE,"E20"),sQuery(id+"F5.wireOp",EDGE,"E21")])],"isStart":true})]});}
            var sketch = newSketch(context, id + "F19", { "sketchPlane" : qUnion([Q0])});
            skCircle(sketch, "E38", {"center": v(0, 0) * mm, "radius": 5.2 * mm});
            skSolve(sketch);
        }
        {
            var Q0;
            Q0=makeQuery(id+"F19.imprint","IMPRINT",FACE,{"disambiguationData":[TD([[makeQuery(id+"F19.imprint","IMPRINT",EDGE,{"derivedFrom":sQuery(id+"F19.wireOp",EDGE,"E38")}),1.0]])]});
            extrude(context, id + "F20", {"entities" : qUnion([Q0]), "operationType" : NewBodyOperationType.REMOVE, "oppositeDirection" : true, "depth" : 4 * mm, "offsetDistance" : 25 * mm});
        }
        {
            var Q0;
            Q0=makeQuery(id+"F20.boolean.opBoolean","COPY",FACE,{"derivedFrom":makeQuery(id+"F20.opExtrude","CAP_FACE",FACE,{"disambiguationData":[OSD([sQuery(id+"F1Hpu5VrwMmlooL_1.wireOp",EDGE,"aa8661ea-3af5-4901-8aae-093f1f5eb203"),sQuery(id+"F19.wireOp",EDGE,"E38")])],"isStart":false})});
            extrude(context, id + "F21", {"entities" : qUnion([Q0]), "depth" : 4 * mm, "offsetDistance" : 25 * mm});
        }
        {
            var Q0;
            Q0=makeQuery(id+"F4.opExtrude","SWEPT_FACE",FACE,{"disambiguationData":[OSD([sQuery(id+"F0.wireOp",EDGE,"E3")])]});
            var sketch = newSketch(context, id + "F22", { "sketchPlane" : qUnion([Q0])});
            skCircle(sketch, "E39", {"center": v(-11.33, -5) * mm, "radius": 1.75 * mm});
            skCircle(sketch, "E40", {"center": v(-11.33, -34) * mm, "radius": 1.75 * mm});
            skCircle(sketch, "E41", {"center": v(11.33, -34) * mm, "radius": 1.75 * mm});
            skCircle(sketch, "E42", {"center": v(11.33, -5) * mm, "radius": 1.75 * mm});
            skCircle(sketch, "E43", {"center": v(-11.33, -34) * mm, "radius": 4 * mm});
            skCircle(sketch, "E44", {"center": v(-11.33, -5) * mm, "radius": 4 * mm});
            skCircle(sketch, "E45", {"center": v(11.33, -5) * mm, "radius": 4 * mm});
            skCircle(sketch, "E46", {"center": v(11.33, -34) * mm, "radius": 4 * mm});
            skLineSegment(sketch, "E47.bottom", {"start": v(11.33, -34) * mm, "end": v(-11.33, -34) * mm, "construction": true});
            skLineSegment(sketch, "E47.top", {"start": v(11.33, -5) * mm, "end": v(-11.33, -5) * mm, "construction": true});
            skLineSegment(sketch, "E47.left", {"start": v(11.33, -34) * mm, "end": v(11.33, -5) * mm, "construction": true});
            skLineSegment(sketch, "E47.right", {"start": v(-11.33, -34) * mm, "end": v(-11.33, -5) * mm, "construction": true});
            skPoint(sketch, "E47.middle", {"position": v(0, -19.5) * mm});
            skPoint(sketch, "E47.middle.positionSnap0", {"position": v(16.33, -19.5) * mm});
            skPoint(sketch, "E47.centerSnap0", {"position": v(16.33, -19.5) * mm});
            skSolve(sketch);
        }
        {
            var Q0;
            Q0=makeQuery(id+"F22.imprint","IMPRINT",FACE,{"disambiguationData":[TD([[makeQuery(id+"F22.imprint","IMPRINT",EDGE,{"derivedFrom":sQuery(id+"F22.wireOp",EDGE,"E39")}),1.0]])]});
            var Q1;
            Q1=makeQuery(id+"F22.imprint","IMPRINT",FACE,{"disambiguationData":[TD([[makeQuery(id+"F22.imprint","IMPRINT",EDGE,{"derivedFrom":sQuery(id+"F22.wireOp",EDGE,"E42")}),1.0]])]});
            var Q2;
            Q2=makeQuery(id+"F22.imprint","IMPRINT",FACE,{"disambiguationData":[TD([[makeQuery(id+"F22.imprint","IMPRINT",EDGE,{"derivedFrom":sQuery(id+"F22.wireOp",EDGE,"E41")}),1.0]])]});
            var Q3;
            Q3=makeQuery(id+"F22.imprint","IMPRINT",FACE,{"disambiguationData":[TD([[makeQuery(id+"F22.imprint","IMPRINT",EDGE,{"derivedFrom":sQuery(id+"F22.wireOp",EDGE,"E40")}),1.0]])]});
            var Q4;
            {var subQ0=sQuery(id+"F5.wireOp",EDGE,"E20");Q4=makeQuery(id+"F7.boolean.opBoolean","MERGE",FACE,{"derivedFrom":[makeQuery(id+"F6.opExtrude","SWEPT_FACE",FACE,{"disambiguationData":[OSD([subQ0])]}),makeQuery(id+"F7.opExtrude","SWEPT_FACE",FACE,{"disambiguationData":[OSD([subQ0])]})]});}
            extrude(context, id + "F23", {"entities" : qUnion([Q0, Q1, Q2, Q3]), "operationType" : NewBodyOperationType.REMOVE, "endBound" : BoundingType.UP_TO_SURFACE, "oppositeDirection" : true, "depth" : 25 * mm, "endBoundEntityFace" : qUnion([Q4]), "offsetDistance" : 25 * mm});
        }
        {
            var Q0;
            Q0=makeQuery(id+"F22.imprint","IMPRINT",FACE,{"disambiguationData":[TD([[makeQuery(id+"F22.imprint","IMPRINT",EDGE,{"derivedFrom":sQuery(id+"F22.wireOp",EDGE,"E40")}),-1.0]])]});
            var Q1;
            Q1=makeQuery(id+"F22.imprint","IMPRINT",FACE,{"disambiguationData":[TD([[makeQuery(id+"F22.imprint","IMPRINT",EDGE,{"derivedFrom":sQuery(id+"F22.wireOp",EDGE,"E41")}),-1.0]])]});
            var Q2;
            Q2=makeQuery(id+"F22.imprint","IMPRINT",FACE,{"disambiguationData":[TD([[makeQuery(id+"F22.imprint","IMPRINT",EDGE,{"derivedFrom":sQuery(id+"F22.wireOp",EDGE,"E42")}),-1.0]])]});
            var Q3;
            Q3=makeQuery(id+"F22.imprint","IMPRINT",FACE,{"disambiguationData":[TD([[makeQuery(id+"F22.imprint","IMPRINT",EDGE,{"derivedFrom":sQuery(id+"F22.wireOp",EDGE,"E39")}),-1.0]])]});
            extrude(context, id + "F24", {"entities" : qUnion([Q0, Q1, Q2, Q3]), "operationType" : NewBodyOperationType.REMOVE, "oppositeDirection" : true, "depth" : 4 * mm, "offsetDistance" : 25 * mm});
        }
        {
            var Q0;
            Q0=makeQuery(id+"F0.imprint","IMPRINT",FACE,{"disambiguationData":[TD([[makeQuery(id+"F0.imprint","IMPRINT",EDGE,{"derivedFrom":sQuery(id+"F0.wireOp",EDGE,"E8")}),1.0]])]});
            extrude(context, id + "F25", {"entities" : qUnion([Q0]), "operationType" : NewBodyOperationType.REMOVE, "depth" : 3 * mm, "offsetDistance" : 25 * mm});
        }
        {
            var Q0;
            {var subQ0=sQuery(id+"F3.wireOp",EDGE,"E17.7");var subQ1=sQuery(id+"F3.wireOp",EDGE,"E17.6");var subQ2=sQuery(id+"F3.wireOp",EDGE,"E17.3");Q0=makeQuery(id+"F6.boolean.opBoolean","MERGE",FACE,{"derivedFrom":[makeQuery(id+"F4.opExtrude","CAP_FACE",FACE,{"disambiguationData":[OSD([sQuery(id+"F0.wireOp",EDGE,"E0"),sQuery(id+"F0.wireOp",EDGE,"E1"),sQuery(id+"F0.wireOp",EDGE,"E2"),sQuery(id+"F0.wireOp",EDGE,"E3"),sQuery(id+"F0.wireOp",EDGE,"E4"),sQuery(id+"F0.wireOp",EDGE,"E5"),sQuery(id+"F0.wireOp",EDGE,"E11"),sQuery(id+"F0.wireOp",EDGE,"E12"),sQuery(id+"F3.wireOp",EDGE,"E17.0"),sQuery(id+"F3.wireOp",EDGE,"E17.1"),sQuery(id+"F3.wireOp",EDGE,"E17.2"),subQ2,sQuery(id+"F3.wireOp",EDGE,"E17.4"),sQuery(id+"F3.wireOp",EDGE,"E17.5"),subQ1,subQ0])],"isStart":false}),makeQuery(id+"F6.opExtrude","CAP_FACE",FACE,{"disambiguationData":[OSD([subQ2,subQ1,subQ0,sQuery(id+"F5.wireOp",EDGE,"E19"),sQuery(id+"F5.wireOp",EDGE,"E20"),sQuery(id+"F5.wireOp",EDGE,"E21")])],"isStart":false})]});}
            var sketch = newSketch(context, id + "F26", { "sketchPlane" : qUnion([Q0])});
            skLineSegment(sketch, "E48", {"start": v(22.5, 21.5) * mm, "end": v(-22.5, 21.5) * mm});
            skSolve(sketch);
        }
        {
            var Q0;
            {var subQ8=makeQuery(id+"F4.opExtrude","CAP_EDGE",EDGE,{"disambiguationData":[OSD([sQuery(id+"F3.wireOp",EDGE,"E17.0")])],"isStart":false});Q0=makeQuery(id+"F26.imprint","IMPRINT",FACE,{"disambiguationData":[TD([[makeQuery(id+"F26.imprint","IMPRINT",EDGE,{"derivedFrom":subQ8}),-1.0]])]});}
            var Q1;
            Q1=makeQuery(id+"F1.opExtrude","CAP_FACE",FACE,{"disambiguationData":[OSD([sQuery(id+"F0.wireOp",EDGE,"E0"),sQuery(id+"F0.wireOp",EDGE,"E1"),sQuery(id+"F0.wireOp",EDGE,"E2"),sQuery(id+"F0.wireOp",EDGE,"E3"),sQuery(id+"F0.wireOp",EDGE,"E4"),sQuery(id+"F0.wireOp",EDGE,"E5"),sQuery(id+"F0.wireOp",EDGE,"E6"),sQuery(id+"F0.wireOp",EDGE,"E7"),sQuery(id+"F0.wireOp",EDGE,"E9"),sQuery(id+"F0.wireOp",EDGE,"E10"),sQuery(id+"F0.wireOp",EDGE,"E11"),sQuery(id+"F0.wireOp",EDGE,"E12"),sQuery(id+"F0.wireOp",EDGE,"E16")])],"isStart":true});
            extrude(context, id + "F27", {"entities" : qUnion([Q0]), "operationType" : NewBodyOperationType.REMOVE, "endBound" : BoundingType.UP_TO_SURFACE, "oppositeDirection" : true, "depth" : 25 * mm, "endBoundEntityFace" : qUnion([Q1]), "offsetDistance" : 25 * mm});
        }
        {
            var Q0;
            Q0=qSketchRegion(id+"F11",true);
            var Q1;
            Q1=sQuery(id+"F9.wireOp",EDGE,"E25");
            var Q2;
            Q2=sQuery(id+"F9.wireOp",EDGE,"E24");
            var Q3;
            Q3=sQuery(id+"F9.wireOp",EDGE,"E26");
            sweep(context, id + "F28", {"profiles" : qUnion([Q0]), "path" : qUnion([Q1, Q2, Q3])});
        }
    });
